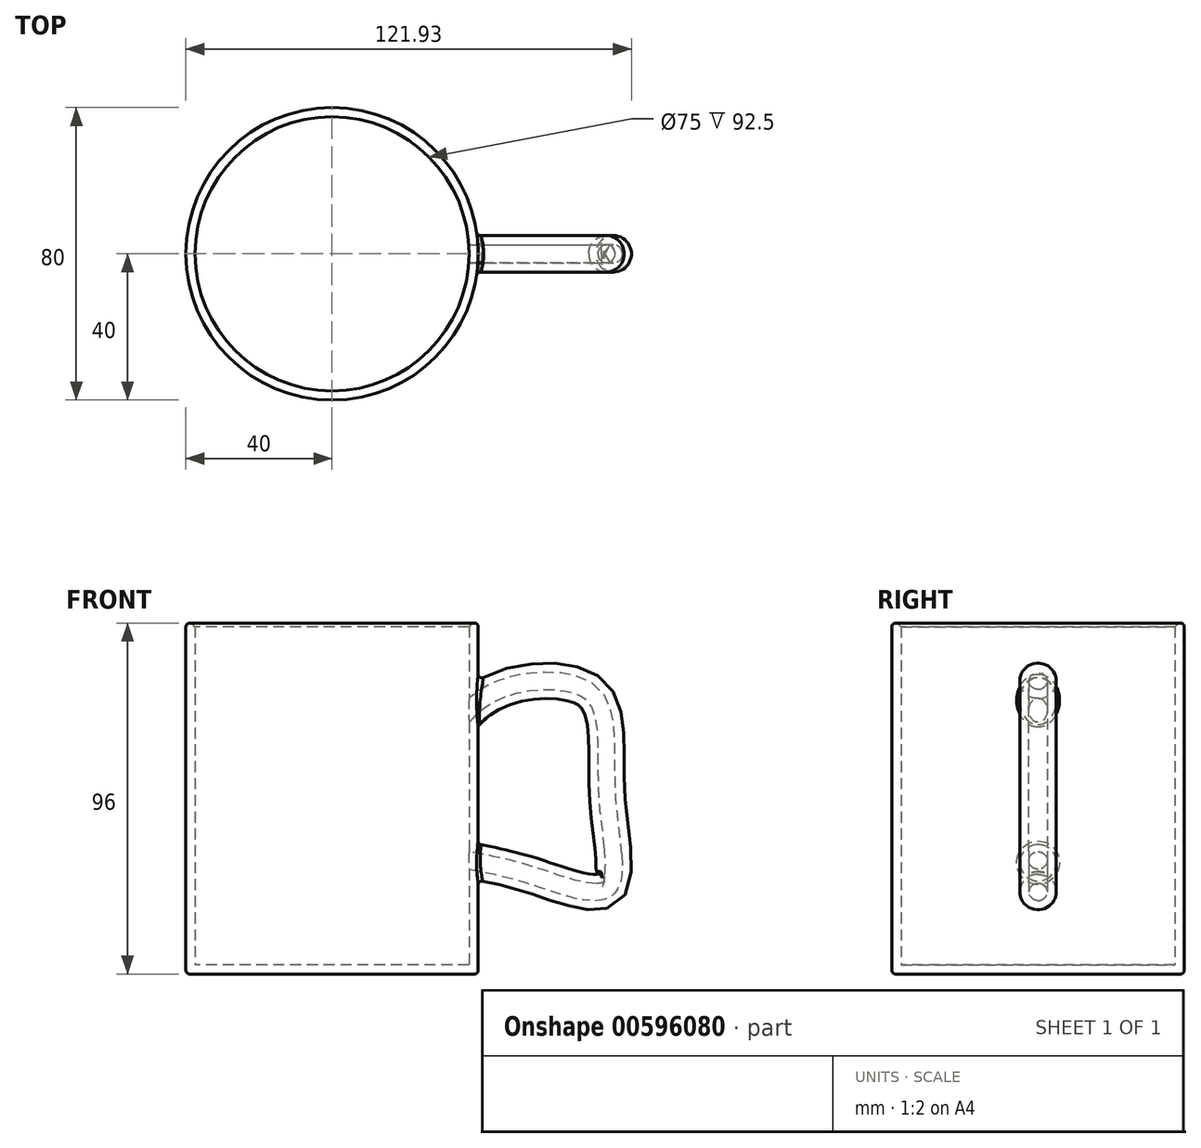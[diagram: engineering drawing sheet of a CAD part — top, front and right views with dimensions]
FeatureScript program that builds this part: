
annotation { "Feature Type Name" : "Feature", "Feature Type Description" : "" }
export const myFeature = defineFeature(function(context is Context, id is Id, definition is map)
    precondition{}
    {
        {
            var Q0;
            Q0=qCreatedBy(makeId("Top.planeOp"),FACE);
            var sketch = newSketch(context, id + "F0", { "sketchPlane" : qUnion([Q0])});
            skCircle(sketch, "E0", {"center": v(0, 0) * mm, "radius": 40 * mm});
            skSolve(sketch);
        }
        {
            var Q0;
            Q0 = qSketchRegion(id + "F0", true);
            extrude(context, id + "F1", {"entities" : qUnion([Q0]), "depth" : 96 * mm, "offsetDistance" : 25 * mm});
        }
        {
            var Q0;
            Q0=qCreatedBy(makeId("Front.planeOp"),FACE);
            var sketch = newSketch(context, id + "F2", { "sketchPlane" : qUnion([Q0])});
            skFitSpline(sketch, "E1", {"points": [v(30.24, 63.74) * mm, v(44.94, 77.95) * mm, v(71.45, 77) * mm, v(75.79, 49.28) * mm, v(75.55, 23.01) * mm, v(54.82, 26.39) * mm, v(35.06, 30.97) * mm], "startDerivative": vector(72.3, 107.18) * mm, "endDerivative": vector(-117.98, 20.98) * mm});
            skSolve(sketch);
        }
        {
            var Q0;
            Q0=qCreatedBy(makeId("Right.planeOp"),FACE);
            cPlane(context, id + "F3", {"entities" : qUnion([Q0]), "cplaneType" : CPlaneType.OFFSET, "offset" : 50 * mm, "width" : 150 * mm, "height" : 150 * mm});
        }
        {
            var Q0;
            Q0=qCreatedBy(id+"F3.planeOp",FACE);
            var sketch = newSketch(context, id + "F4", { "sketchPlane" : qUnion([Q0])});
            skCircle(sketch, "E2", {"center": v(0, 79.1) * mm, "radius": 5 * mm});
            skSolve(sketch);
        }
        {
            var Q0;
            Q0=makeQuery(id+"F4.imprint","IMPRINT",FACE,{"disambiguationData":[TD([[makeQuery(id+"F4.imprint","IMPRINT",EDGE,{"derivedFrom":sQuery(id+"F4.wireOp",EDGE,"E2")}),1.0]])]});
            var Q1;
            Q1=sQuery(id+"F2.wireOp",EDGE,"E1");
            sweep(context, id + "F5", {"operationType" : NewBodyOperationType.ADD, "profiles" : qUnion([Q0]), "path" : qUnion([Q1])});
        }
        {
            var Q0;
            Q0=makeQuery(id+"F1.opExtrude","CAP_FACE",FACE,{"disambiguationData":[OSD([sQuery(id+"F0.wireOp",EDGE,"E0")])],"isStart":false});
            shell(context, id + "F6", {"entities" : qUnion([Q0]), "thickness" : 2.5 * mm});
        }
        {
            var Q0;
            Q0=makeQuery(id+"F1.opExtrude","CAP_EDGE",EDGE,{"disambiguationData":[OSD([sQuery(id+"F0.wireOp",EDGE,"E0")])],"isStart":false});
            fillet(context, id + "F7", {"entities" : qUnion([Q0]), "radius" : 1 * mm, "tangentPropagation" : true, "allowEdgeOverflow" : false});
        }
        {
            var Q0;
            Q0=makeQuery(id+"F5.opSweep","SWEPT_FACE",FACE,{"disambiguationData":[OSD([sQuery(id+"F2.wireOp",EDGE,"E1"),sQuery(id+"F4.wireOp",EDGE,"E2")])]});
            fillet(context, id + "F8", {"entities" : qUnion([Q0]), "radius" : 1 * mm, "tangentPropagation" : true, "allowEdgeOverflow" : false});
        }
        {
            var Q0;
            Q0=makeQuery(id+"F1.opExtrude","CAP_EDGE",EDGE,{"disambiguationData":[OSD([sQuery(id+"F0.wireOp",EDGE,"E0")])],"isStart":true});
            fillet(context, id + "F9", {"entities" : qUnion([Q0]), "radius" : 1 * mm, "tangentPropagation" : true, "allowEdgeOverflow" : false});
        }
        {
            var Q0;
            {var subQ0=sQuery(id+"F0.wireOp",EDGE,"E0");Q0=makeQuery(id+"F6.opShell","OFFSET_EDGE",EDGE,{"disambiguationData":[OSD([subQ0]),TDD([makeQuery(id+"F1.opExtrude","CAP_EDGE",EDGE,{"disambiguationData":[OSD([subQ0])],"isStart":false})])]});}
            chamfer(context, id + "F10", {"entities" : qUnion([Q0]), "width" : 1 * mm, "tangentPropagation" : true});
        }
        {
            var Q0;
            {var subQ0=sQuery(id+"F0.wireOp",EDGE,"E0");Q0=makeQuery(id+"F10.opChamfer","BLEND_EDGE",EDGE,{"blendedFrom":[makeQuery(id+"F6.opShell","OFFSET_EDGE",EDGE,{"disambiguationData":[OSD([subQ0]),TDD([makeQuery(id+"F1.opExtrude","CAP_EDGE",EDGE,{"disambiguationData":[OSD([subQ0])],"isStart":false})])]}),makeQuery(id+"F1.opExtrude","CAP_FACE",FACE,{"disambiguationData":[OSD([subQ0])],"isStart":false})],"blendedInto":[makeQuery(id+"F1.opExtrude","CAP_FACE",FACE,{"disambiguationData":[OSD([subQ0])],"isStart":false})]});}
            var Q1;
            {var subQ0=sQuery(id+"F0.wireOp",EDGE,"E0");Q1=makeQuery(id+"F7.opFillet","BLEND_EDGE",EDGE,{"blendedFrom":[makeQuery(id+"F1.opExtrude","CAP_EDGE",EDGE,{"disambiguationData":[OSD([subQ0])],"isStart":false}),makeQuery(id+"F1.opExtrude","CAP_FACE",FACE,{"disambiguationData":[OSD([subQ0])],"isStart":false})],"blendedInto":[makeQuery(id+"F1.opExtrude","CAP_FACE",FACE,{"disambiguationData":[OSD([subQ0])],"isStart":false})]});}
            fillet(context, id + "F11", {"entities" : qUnion([Q0, Q1]), "radius" : 1 * mm, "tangentPropagation" : true, "allowEdgeOverflow" : false});
        }
    });
